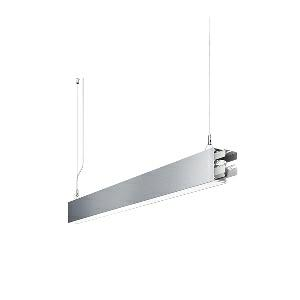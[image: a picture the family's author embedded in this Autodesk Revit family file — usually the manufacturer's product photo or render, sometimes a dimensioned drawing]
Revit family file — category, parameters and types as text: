
# Revit family: idoo_line_-_ilp_2000_830_d_sta_00805717_1903
name_source: partatom
category: Lighting Fixtures
units: mm (PartAtom-declared; Revit-internal decimal feet)

## family parameters
Cut with Voids When Loaded = No
Host = Face
Light Source = No
Part Type = Normal
Room Calculation Point = No
Round Connector Dimension = Use Diameter
Shared = No

## types (1)
- IDOO.line - ILP 2000/830/D STA (1 x LED, 2250 lm, 3000K)
    Apparent Load = 17 VA
    Approval mark = CE
    CIE Flux Codes = 66 91 98 40 100
    Color Rendering = 80-89
    Color Temperature = 3000K
    Control Gear = Electronic ballast
    Default Elevation = 1800 mm
    Description = ILP 2000/830/D|Suspended luminaire|light source: LED|connected load: 220-240 V, 50/60 Hz|Power consumption: approx. 17 W|standby: approx. 0,20|luminous flux: 2250 lm|luminous efficacy: 132 lm/W|light distribution: Direct/indirect|direct ratio: approx. 40 %|colour temperature: Warm white, ca. 3000 K|color rendering index (CRI): >= 80|chromaticity tolerance:  3 SDCM|System of protection: IP 40|technology: Continuously dimmable|luminaire body|material: Sectional aluminium|colour: Silver|lamp cover: Acrylic (PMMA), Clear|mains lead: 2.00 m With free stranded wires|Fastening: Steel cable 0.3 - 0.7 m|glare control: Prism aperture|luminance(L65): <= 2700 cd/m|unified glare rating(4H 8H): <=  16|special features: DALI Load 1x, TouchDIM - dimming via standard switch, Through-wired, up to 18 m on one mains connection, Flicker-free, Suitable as emergency lighting, Start luminaire with mains connection, Mechanical and electrical connection of the individual modules without tools|
    Frequency = 50 Hz
    Height = 110 mm
    Lamp = 1 x LED
    Lamp Light Flux = 2250 lm
    Lamp count = 1
    Length = 848 mm
    Luminous efficacy = 132 lm/W
    Manufacturer = Waldmann
    ModVariant = No
    Model = 00805717
    Mounting Place = Ceiling
    Mounting Type = Pendant
    Number of Poles = 1
    OnlyDefault = Yes
    Power Factor = 1
    Product Name = IDOO.line - ILP 2000/830/D STA
    Product group = Suspended luminaire
    ProductGroupID = 9
    Protection Class = Protection class I
    Protection Degree = IP 40
    RLX_Detail_Level = 1
    RLX_Emergency_Light_Flux = 0 lm
    RLX_Emergency_Type = 0
    RLX_Emergency_Type_DB = No
    RlxData = <blob elided: 20769 chars, md5=989a916c>
    Socket = socket
    Standby Power = 0 W
    System Light Flux = 2250 lm
    System Power = 17 W
    Type Comments = Product without accessories
    Type Image = 113298000-00692558.jpg
    URL = http://relux.com
    VarID = ---
    Voltage = 230 V
    Voltage Range = 220-240 V
    Weight = 0.00 kg
    Width = 60 mm  [stored 0.19685 ft]

note: [stored X ft] marks values corroborated as IEEE doubles in the binary element streams (Revit-internal decimal feet)

## geometry (parser evidence)
native form markers: Blend x4, Sweep x12
no freeform markers — native parametric forms only
